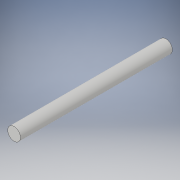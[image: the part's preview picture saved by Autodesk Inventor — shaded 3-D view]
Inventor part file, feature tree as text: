
AUTODESK INVENTOR PART (.ipt)
format: ipt  version: 2018 (Build 220112000, 112)  size: 90,624 bytes
history: native  units: in
note: dims shown in document units (in); Inventor stores cm internally (conversion verified against a paired STEP export)
features: extrude x1, sketch x1
ambient origin geometry x8: Origin, YZ Plane, XZ Plane, XY Plane, X Axis, Y Axis, Z Axis, Center Point
bodies: Solid1 (feature_tree)
feature tree (2):
  extrude  "Extrusion1"  Depth=5.9055in TaperAngle=0.0deg
  sketch  "Sketch1"  dims[d0=0.5in d1=5.9055in d2=0.0in]
